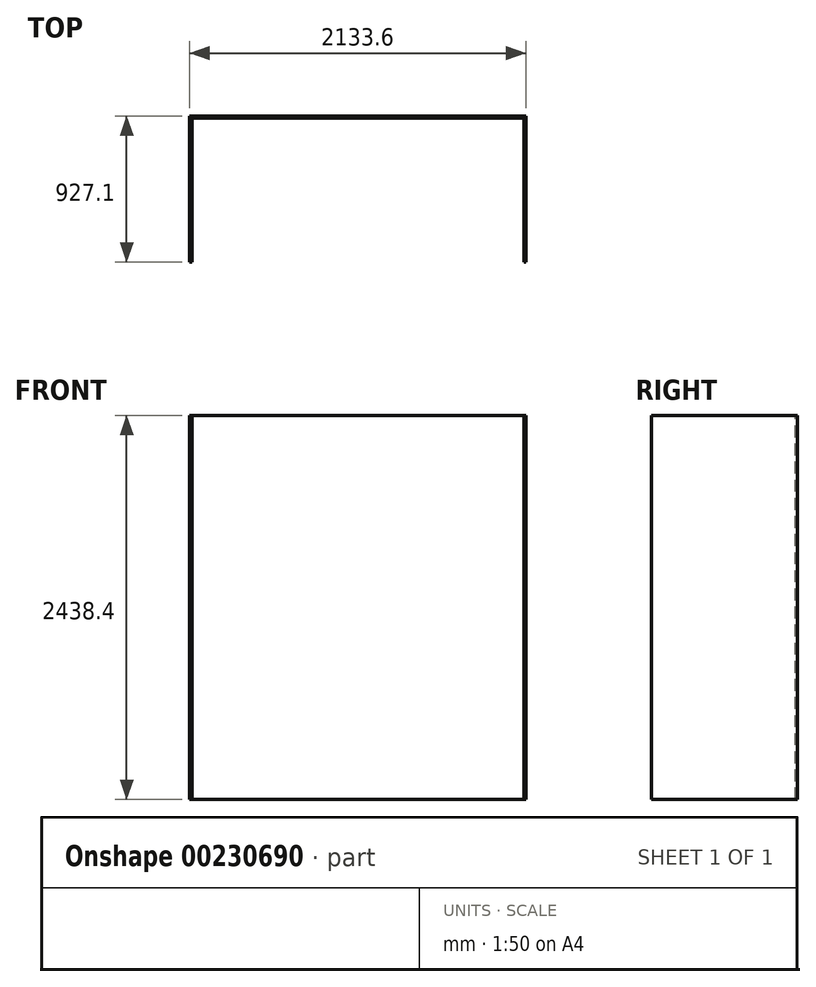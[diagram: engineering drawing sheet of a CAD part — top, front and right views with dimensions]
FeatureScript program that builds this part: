
annotation { "Feature Type Name" : "Feature", "Feature Type Description" : "" }
export const myFeature = defineFeature(function(context is Context, id is Id, definition is map)
    precondition{}
    {
        {
            var Q0;
            Q0=qCreatedBy(makeId("Top.planeOp"),FACE);
            var sketch = newSketch(context, id + "F0", { "sketchPlane" : qUnion([Q0])});
            skLineSegment(sketch, "E0.bottom", {"start": v(-1051.93, 340.04) * mm, "end": v(1081.67, 340.04) * mm});
            skLineSegment(sketch, "E0.top", {"start": v(-1051.93, -587.06) * mm, "end": v(1081.67, -587.06) * mm});
            skLineSegment(sketch, "E0.left", {"start": v(-1051.93, 340.04) * mm, "end": v(-1051.93, -587.06) * mm});
            skLineSegment(sketch, "E0.right", {"start": v(1081.67, 340.04) * mm, "end": v(1081.67, -587.06) * mm});
            skSolve(sketch);
        }
        {
            var Q0;
            Q0=makeQuery(id+"F0.imprint","IMPRINT",FACE,{"disambiguationData":[TD([[makeQuery(id+"F0.imprint","IMPRINT",EDGE,{"derivedFrom":sQuery(id+"F0.wireOp",EDGE,"E0.bottom")}),-1.0]])]});
            extrude(context, id + "F1", {"entities" : qUnion([Q0]), "oppositeDirection" : true, "depth" : 2438.4 * mm});
        }
        {
            var Q0;
            Q0=makeQuery(id+"F1.opExtrude","CAP_FACE",FACE,{"disambiguationData":[OSD([sQuery(id+"F0.wireOp",EDGE,"E0.bottom"),sQuery(id+"F0.wireOp",EDGE,"E0.top"),sQuery(id+"F0.wireOp",EDGE,"E0.left"),sQuery(id+"F0.wireOp",EDGE,"E0.right")])],"isStart":true});
            var Q1;
            Q1=makeQuery(id+"F1.opExtrude","SWEPT_FACE",FACE,{"disambiguationData":[OSD([sQuery(id+"F0.wireOp",EDGE,"E0.top")])]});
            var Q2;
            Q2=makeQuery(id+"F1.opExtrude","CAP_FACE",FACE,{"disambiguationData":[OSD([sQuery(id+"F0.wireOp",EDGE,"E0.bottom"),sQuery(id+"F0.wireOp",EDGE,"E0.top"),sQuery(id+"F0.wireOp",EDGE,"E0.left"),sQuery(id+"F0.wireOp",EDGE,"E0.right")])],"isStart":false});
            shell(context, id + "F2", {"entities" : qUnion([Q0, Q1, Q2]), "thickness" : 12.7 * mm});
        }
    });
